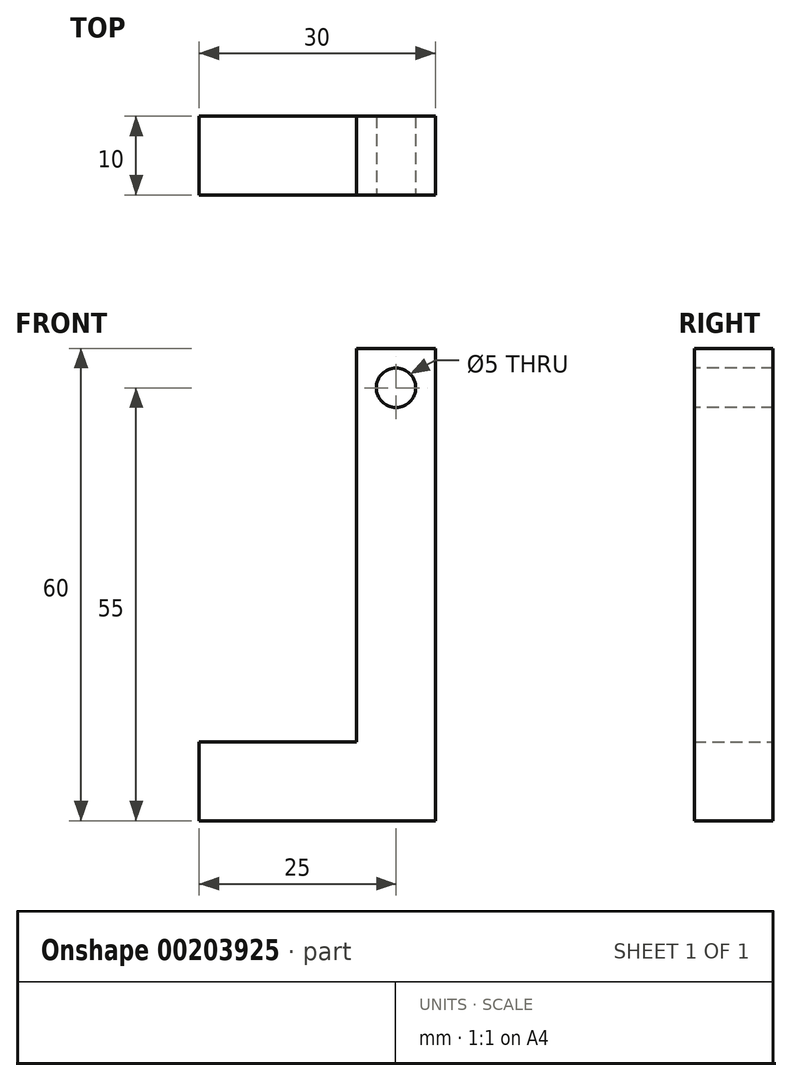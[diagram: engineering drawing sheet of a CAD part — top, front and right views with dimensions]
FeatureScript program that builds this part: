
annotation { "Feature Type Name" : "Feature", "Feature Type Description" : "" }
export const myFeature = defineFeature(function(context is Context, id is Id, definition is map)
    precondition{}
    {
        {
            var Q0;
            Q0=qCreatedBy(makeId("Front.planeOp"),FACE);
            var sketch = newSketch(context, id + "F0", { "sketchPlane" : qUnion([Q0])});
            skLineSegment(sketch, "E0.bottom", {"start": v(5, 25) * mm, "end": v(-5, 25) * mm});
            skLineSegment(sketch, "E0.top", {"start": v(5, -25) * mm, "end": v(-5, -25) * mm});
            skLineSegment(sketch, "E0.left", {"start": v(5, 25) * mm, "end": v(5, -25) * mm});
            skLineSegment(sketch, "E0.right", {"start": v(-5, 25) * mm, "end": v(-5, -25) * mm});
            skPoint(sketch, "E0.middle", {"position": v(0, 0) * mm});
            skLineSegment(sketch, "E1.bottom", {"start": v(5, -25) * mm, "end": v(-25, -25) * mm});
            skLineSegment(sketch, "E1.top", {"start": v(5, -35) * mm, "end": v(-25, -35) * mm});
            skLineSegment(sketch, "E1.left", {"start": v(5, -25) * mm, "end": v(5, -35) * mm});
            skLineSegment(sketch, "E1.right", {"start": v(-25, -25) * mm, "end": v(-25, -35) * mm});
            skSolve(sketch);
        }
        {
            var Q0;
            Q0=qSketchRegion(id+"F0",true);
            extrude(context, id + "F1", {"entities" : qUnion([Q0]), "depth" : 10 * mm});
        }
        {
            var Q0;
            Q0=makeQuery(id+"F1.opExtrude","CAP_FACE",FACE,{"disambiguationData":[OSD([sQuery(id+"F0.wireOp",EDGE,"E0.bottom"),sQuery(id+"F0.wireOp",EDGE,"E0.left"),sQuery(id+"F0.wireOp",EDGE,"E0.right"),sQuery(id+"F0.wireOp",EDGE,"E1.bottom"),sQuery(id+"F0.wireOp",EDGE,"E1.top"),sQuery(id+"F0.wireOp",EDGE,"E1.left"),sQuery(id+"F0.wireOp",EDGE,"E1.right")])],"isStart":false});
            var sketch = newSketch(context, id + "F2", { "sketchPlane" : qUnion([Q0])});
            skCircle(sketch, "E2", {"center": v(0, 20) * mm, "radius": 2.5 * mm});
            skSolve(sketch);
        }
        {
            var Q0;
            Q0=qSketchRegion(id+"F2",true);
            extrude(context, id + "F3", {"entities" : qUnion([Q0]), "operationType" : NewBodyOperationType.REMOVE, "endBound" : BoundingType.UP_TO_NEXT, "oppositeDirection" : true, "depth" : 25 * mm});
        }
    });
